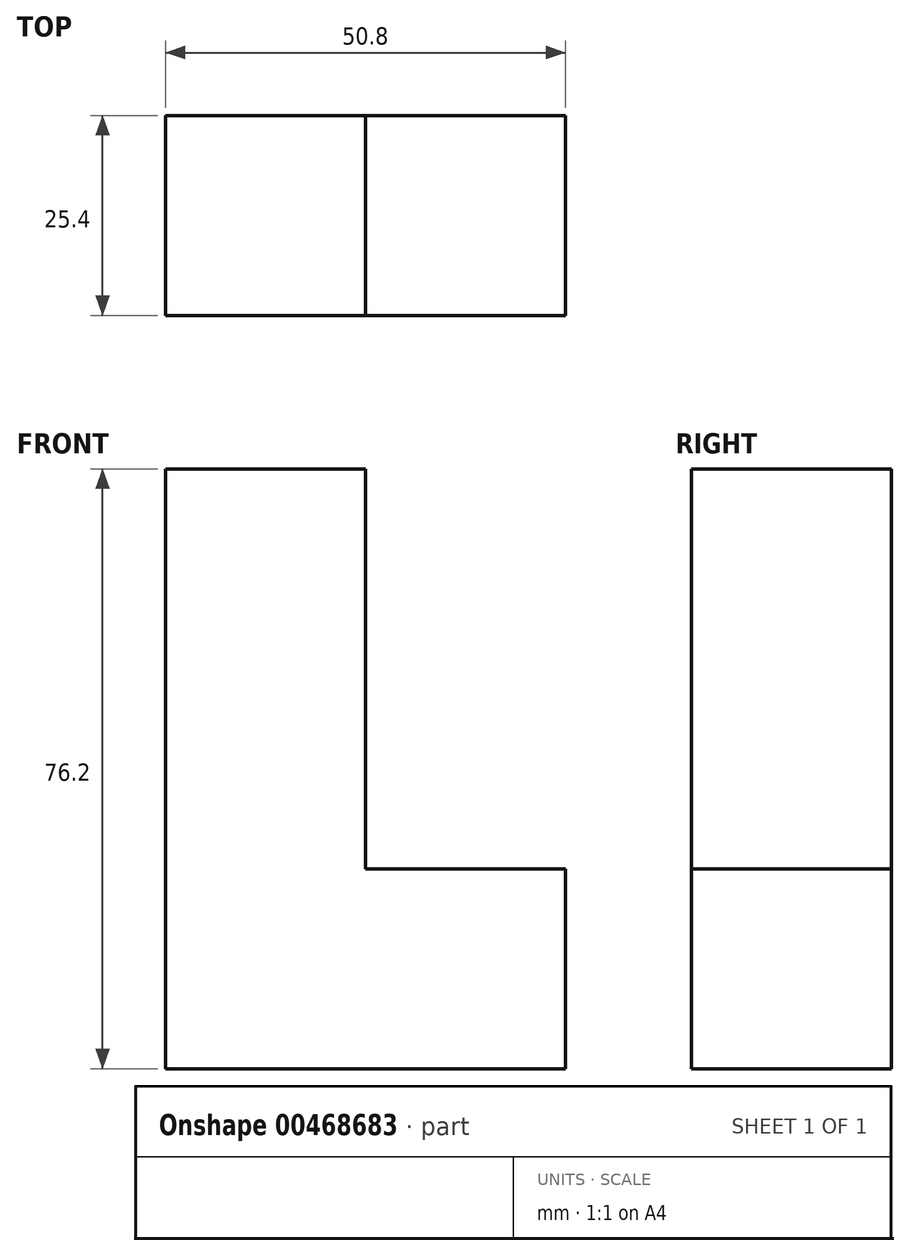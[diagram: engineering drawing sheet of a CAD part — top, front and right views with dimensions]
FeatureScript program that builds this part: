
annotation { "Feature Type Name" : "Feature", "Feature Type Description" : "" }
export const myFeature = defineFeature(function(context is Context, id is Id, definition is map)
    precondition{}
    {
        {
            var Q0;
            Q0=qCreatedBy(makeId("Front.planeOp"),FACE);
            var sketch = newSketch(context, id + "F0", { "sketchPlane" : qUnion([Q0])});
            skLineSegment(sketch, "E0.bottom", {"start": v(-25.4, 41.6) * mm, "end": v(0, 41.6) * mm});
            skLineSegment(sketch, "E0.top", {"start": v(-25.4, -34.6) * mm, "end": v(0, -34.6) * mm});
            skLineSegment(sketch, "E0.left", {"start": v(-25.4, 41.6) * mm, "end": v(-25.4, -34.6) * mm});
            skLineSegment(sketch, "E1.bottom", {"start": v(0, -34.6) * mm, "end": v(25.4, -34.6) * mm});
            skLineSegment(sketch, "E1.top", {"start": v(0, -9.2) * mm, "end": v(25.4, -9.2) * mm});
            skLineSegment(sketch, "E1.right", {"start": v(25.4, -34.6) * mm, "end": v(25.4, -9.2) * mm});
            skLineSegment(sketch, "E2", {"start": v(0, -9.2) * mm, "end": v(0, 41.6) * mm});
            skSolve(sketch);
        }
        {
            var Q0;
            Q0=makeQuery(id+"F0.imprint","IMPRINT",FACE,{"disambiguationData":[TD([[makeQuery(id+"F0.imprint","IMPRINT",EDGE,{"derivedFrom":sQuery(id+"F0.wireOp",EDGE,"E0.bottom")}),-1.0]])]});
            extrude(context, id + "F1", {"entities" : qUnion([Q0]), "depth" : 25.4 * mm});
        }
    });
